# Revit family: Kew
name_source: partatom
category: Lighting Fixtures
revit_build: Autodesk Revit LT 2015 (Build: 20140606_1530(x64)
units: mm (PartAtom-declared; Revit-internal decimal feet)

## types (1)
- Kew/1W/350mA/927/Olive Green
    BIMObjectName = Kew
    BallastCELMAEnergyEfficiencyIndex = See driver specification
    Beam Width = Narrow
    CableLength = 5000 mm  [stored 16.4042 ft]
    CableSize = 6mm OD - 2 off 24/0.2 Tinned Copper Wire
    CableType = 2 Core Silicon
    CodePerformance = GLKW27251
    Color = Olive Green
    Color Filter = 16777215
    CurrentRating = 350mA
    Description = Miniature directional spotlight with ground spike
    Dimming Lamp Color Temperature Shift = <None>
    DurationUnit = year
    Efficacy = 63 lm/W
    ExpectedLife = Lifetime L70/B10 >50,000 hrs
    Finish = Olive Green
    ForwardVoltage = 2.8V DC
    IngressProtection = IP67
    InsulationStandardClass = Class III
    Keynote = Technical data figures are for guidance only and are subject to ±5% tolerance
    LampColourRendering = ≥90 Ra
    LampColourTemperature = 2700K
    LampLumens = 84 lm
    LampType = LED
    LuminaireLumens = 63 lm
    Manufacturer = John Cullen Lighting Ltd
    ManufacturerName = John Cullen Lighting Ltd
    ManufacturerURL = www.johncullenlighting.co.uk
    Material = Aluminium
    MaxAmbientTemperature = 50.00°
    Model = Kew
    ModelNumber = GLKW27251
    NBSDescription = General purpose luminaires are described by characteristics such as standards, photometric performance and supply circuit conductor connections.
An example use may be within a hard wired general lighting system.
    Name = Kew
    NominalHeight = 500 mm  [stored 1.64042 ft]
    NominalLength = 62 mm  [stored 0.203412 ft]
    NominalWidth = 31 mm  [stored 0.101706 ft]
    Photometric Web File = Kew-350.IES
    ProductInformation = http://www.johncullenlighting.co.uk
    Size = 110xD31x500
    Tilt Angle = 0.00°
    URL = http://www.johncullenlighting.co.uk
    Uniclass2 = Pr_70_70_48_35 Ground mounted luminaires
    Version = 1
    WarrantyDescription = Refer to John Cullen Lighting Ltd - Terms and Conditions document
    WarrantyDurationLabor = www.johncullenlighting.co.uk/terms_and_conditions/
    WarrantyDurationParts = www.johncullenlighting.co.uk/terms_and_conditions/
    WarrantyDurationUnit = www.johncullenlighting.co.uk/terms_and_conditions/
    WarrantyGuarantorLabor = www.johncullenlighting.co.uk/terms_and_conditions/
    WarrantyGuarantorParts = www.johncullenlighting.co.uk/terms_and_conditions/
    Wattage = 1 W
    Weight = 480

note: [stored X ft] marks values corroborated as IEEE doubles in the binary element streams (Revit-internal decimal feet)

## geometry (parser evidence)
native form markers: Sweep x3
no freeform markers — native parametric forms only
